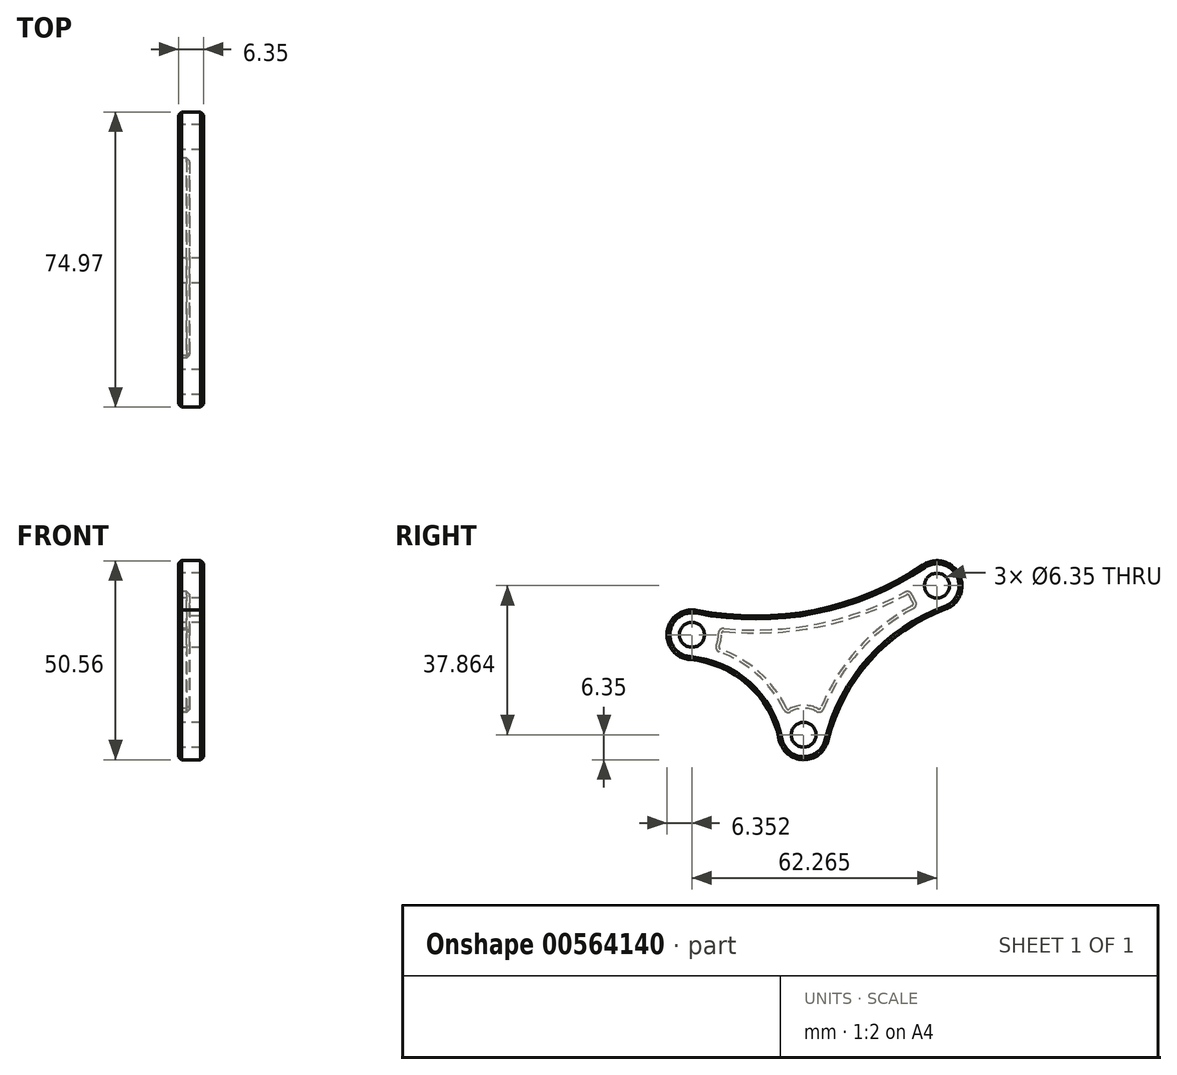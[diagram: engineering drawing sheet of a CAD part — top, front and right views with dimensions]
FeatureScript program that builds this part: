
annotation { "Feature Type Name" : "Feature", "Feature Type Description" : "" }
export const myFeature = defineFeature(function(context is Context, id is Id, definition is map)
    precondition{}
    {
        {
            var Q0;
            Q0=qCreatedBy(makeId("Right.planeOp"),FACE);
            var sketch = newSketch(context, id + "F0", { "sketchPlane" : qUnion([Q0])});
            skCircle(sketch, "E0", {"center": v(0, 0) * mm, "radius": 3.18 * mm});
            skCircle(sketch, "E1", {"center": v(33.87, 37.86) * mm, "radius": 3.18 * mm});
            skCircle(sketch, "E2", {"center": v(-28.4, 25.4) * mm, "radius": 3.18 * mm});
            skCircle(sketch, "E3", {"center": v(-28.4, 25.4) * mm, "radius": 6.35 * mm});
            skCircle(sketch, "E4", {"center": v(33.87, 37.86) * mm, "radius": 6.35 * mm});
            skCircle(sketch, "E5", {"center": v(0, 0) * mm, "radius": 6.35 * mm});
            skLineSegment(sketch, "E6", {"start": v(-28.4, 25.4) * mm, "end": v(33.87, 37.86) * mm});
            skLineSegment(sketch, "E7", {"start": v(0, 0) * mm, "end": v(-28.4, 25.4) * mm});
            skLineSegment(sketch, "E8", {"start": v(33.87, 37.86) * mm, "end": v(0, 0) * mm});
            skArc(sketch, "E9", {"start": v(-27.15, 31.63) * mm, "mid": v(2.73, 31.63) * mm, "end": v(30.32, 43.13) * mm});
            skArc(sketch, "E10", {"start": v(-6.23, -1.25) * mm, "mid": v(-14.2, 12.7) * mm, "end": v(-28.94, 19.07) * mm});
            skArc(sketch, "E11", {"start": v(36.05, 31.9) * mm, "mid": v(16.93, 18.93) * mm, "end": v(6.17, -1.5) * mm});
            skSolve(sketch);
        }
        {
            var Q0;
            {var subQ0=sQuery(id+"F0.wireOp",EDGE,"E9");var subQ1=sQuery(id+"F0.wireOp",EDGE,"E3");var subQ2=makeQuery(id+"F0.imprint","INTERSECT",VERTEX,{"derivedFrom":[subQ1,subQ0]});Q0=makeQuery(id+"F0.imprint","IMPRINT",FACE,{"disambiguationData":[TD([[makeQuery(id+"F0.imprint","IMPRINT",EDGE,{"disambiguationData":[TD([[subQ2,1.0]])],"derivedFrom":subQ1}),-1.0]])]});}
            var Q1;
            {var subQ0=sQuery(id+"F0.wireOp",EDGE,"E10");var subQ1=sQuery(id+"F0.wireOp",EDGE,"E3");var subQ2=makeQuery(id+"F0.imprint","INTERSECT",VERTEX,{"derivedFrom":[subQ1,subQ0]});Q1=makeQuery(id+"F0.imprint","IMPRINT",FACE,{"disambiguationData":[TD([[makeQuery(id+"F0.imprint","IMPRINT",EDGE,{"disambiguationData":[TD([[subQ2,-1.0]])],"derivedFrom":subQ1}),-1.0]])]});}
            var Q2;
            {var subQ0=sQuery(id+"F0.wireOp",EDGE,"E9");var subQ1=sQuery(id+"F0.wireOp",EDGE,"E4");var subQ2=makeQuery(id+"F0.imprint","INTERSECT",VERTEX,{"derivedFrom":[subQ1,subQ0]});Q2=makeQuery(id+"F0.imprint","IMPRINT",FACE,{"disambiguationData":[TD([[makeQuery(id+"F0.imprint","IMPRINT",EDGE,{"disambiguationData":[TD([[subQ2,-1.0]])],"derivedFrom":subQ1}),-1.0]])]});}
            var Q3;
            {var subQ0=sQuery(id+"F0.wireOp",EDGE,"E10");var subQ1=sQuery(id+"F0.wireOp",EDGE,"E5");var subQ2=makeQuery(id+"F0.imprint","INTERSECT",VERTEX,{"derivedFrom":[subQ1,subQ0]});Q3=makeQuery(id+"F0.imprint","IMPRINT",FACE,{"disambiguationData":[TD([[makeQuery(id+"F0.imprint","IMPRINT",EDGE,{"disambiguationData":[TD([[subQ2,1.0]])],"derivedFrom":subQ1}),-1.0]])]});}
            var Q4;
            {var subQ5=sQuery(id+"F0.wireOp",EDGE,"E7");var subQ6=sQuery(id+"F0.wireOp",EDGE,"E0");var subQ7=makeQuery(id+"F0.imprint","INTERSECT",VERTEX,{"derivedFrom":[subQ6,subQ5]});Q4=makeQuery(id+"F0.imprint","IMPRINT",FACE,{"disambiguationData":[TD([[makeQuery(id+"F0.imprint","IMPRINT",EDGE,{"disambiguationData":[TD([[subQ7,-1.0]])],"derivedFrom":subQ6}),-1.0]])]});}
            var Q5;
            {var subQ5=sQuery(id+"F0.wireOp",EDGE,"E6");var subQ7=sQuery(id+"F0.wireOp",EDGE,"E1");var subQ8=makeQuery(id+"F0.imprint","INTERSECT",VERTEX,{"derivedFrom":[subQ7,subQ5]});Q5=makeQuery(id+"F0.imprint","IMPRINT",FACE,{"disambiguationData":[TD([[makeQuery(id+"F0.imprint","IMPRINT",EDGE,{"disambiguationData":[TD([[subQ8,1.0]])],"derivedFrom":subQ7}),-1.0]])]});}
            var Q6;
            {var subQ4=sQuery(id+"F0.wireOp",EDGE,"E6");var subQ5=sQuery(id+"F0.wireOp",EDGE,"E2");var subQ6=makeQuery(id+"F0.imprint","INTERSECT",VERTEX,{"derivedFrom":[subQ5,subQ4]});Q6=makeQuery(id+"F0.imprint","IMPRINT",FACE,{"disambiguationData":[TD([[makeQuery(id+"F0.imprint","IMPRINT",EDGE,{"disambiguationData":[TD([[subQ6,-1.0]])],"derivedFrom":subQ5}),-1.0]])]});}
            var Q7;
            {var subQ0=sQuery(id+"F0.wireOp",EDGE,"E6");var subQ2=sQuery(id+"F0.wireOp",EDGE,"E3");var subQ3=makeQuery(id+"F0.imprint","INTERSECT",VERTEX,{"derivedFrom":[subQ2,subQ0]});Q7=makeQuery(id+"F0.imprint","IMPRINT",FACE,{"disambiguationData":[TD([[makeQuery(id+"F0.imprint","IMPRINT",EDGE,{"disambiguationData":[TD([[subQ3,1.0]])],"derivedFrom":subQ2}),-1.0]])]});}
            var Q8;
            {var subQ0=sQuery(id+"F0.wireOp",EDGE,"E6");var subQ1=sQuery(id+"F0.wireOp",EDGE,"E2");var subQ2=makeQuery(id+"F0.imprint","INTERSECT",VERTEX,{"derivedFrom":[subQ1,subQ0]});Q8=makeQuery(id+"F0.imprint","IMPRINT",FACE,{"disambiguationData":[TD([[makeQuery(id+"F0.imprint","IMPRINT",EDGE,{"disambiguationData":[TD([[subQ2,1.0]])],"derivedFrom":subQ1}),-1.0]])]});}
            var Q9;
            {var subQ0=sQuery(id+"F0.wireOp",EDGE,"E6");var subQ1=sQuery(id+"F0.wireOp",EDGE,"E1");var subQ2=makeQuery(id+"F0.imprint","INTERSECT",VERTEX,{"derivedFrom":[subQ1,subQ0]});Q9=makeQuery(id+"F0.imprint","IMPRINT",FACE,{"disambiguationData":[TD([[makeQuery(id+"F0.imprint","IMPRINT",EDGE,{"disambiguationData":[TD([[subQ2,-1.0]])],"derivedFrom":subQ1}),-1.0]])]});}
            var Q10;
            {var subQ0=sQuery(id+"F0.wireOp",EDGE,"E7");var subQ1=sQuery(id+"F0.wireOp",EDGE,"E0");var subQ2=makeQuery(id+"F0.imprint","INTERSECT",VERTEX,{"derivedFrom":[subQ1,subQ0]});Q10=makeQuery(id+"F0.imprint","IMPRINT",FACE,{"disambiguationData":[TD([[makeQuery(id+"F0.imprint","IMPRINT",EDGE,{"disambiguationData":[TD([[subQ2,1.0]])],"derivedFrom":subQ1}),-1.0]])]});}
            var Q11;
            {var subQ0=sQuery(id+"F0.wireOp",EDGE,"E11");var subQ1=sQuery(id+"F0.wireOp",EDGE,"E5");var subQ2=makeQuery(id+"F0.imprint","INTERSECT",VERTEX,{"derivedFrom":[subQ1,subQ0]});Q11=makeQuery(id+"F0.imprint","IMPRINT",FACE,{"disambiguationData":[TD([[makeQuery(id+"F0.imprint","IMPRINT",EDGE,{"disambiguationData":[TD([[subQ2,-1.0]])],"derivedFrom":subQ1}),-1.0]])]});}
            var Q12;
            {var subQ0=sQuery(id+"F0.wireOp",EDGE,"E11");var subQ1=sQuery(id+"F0.wireOp",EDGE,"E4");var subQ2=makeQuery(id+"F0.imprint","INTERSECT",VERTEX,{"derivedFrom":[subQ1,subQ0]});Q12=makeQuery(id+"F0.imprint","IMPRINT",FACE,{"disambiguationData":[TD([[makeQuery(id+"F0.imprint","IMPRINT",EDGE,{"disambiguationData":[TD([[subQ2,1.0]])],"derivedFrom":subQ1}),-1.0]])]});}
            var Q13;
            {var subQ7=sQuery(id+"F0.wireOp",EDGE,"s0z4VmjC-9Jtz-9oDN-pM9U-WHnKUmS6Y34w");Q13=makeQuery(id+"F0.imprint","IMPRINT",FACE,{"disambiguationData":[TD([[makeQuery(id+"F0.imprint","IMPRINT",EDGE,{"derivedFrom":subQ7}),-1.0]])]});}
            var Q14;
            {var subQ3=sQuery(id+"F0.wireOp",EDGE,"DwXPQsX5-wXzO-8GNt-yisA-XoadTiBy5RnP");Q14=makeQuery(id+"F0.imprint","IMPRINT",FACE,{"disambiguationData":[TD([[makeQuery(id+"F0.imprint","IMPRINT",EDGE,{"derivedFrom":subQ3}),1.0]])]});}
            extrude(context, id + "F1", {"entities" : qUnion([Q0, Q1, Q2, Q3, Q4, Q5, Q6, Q7, Q8, Q9, Q10, Q11, Q12, Q13, Q14]), "depth" : 6.35 * mm, "offsetDistance" : 25.4 * mm});
        }
        {
            var Q0;
            Q0=makeQuery(id+"F1.opExtrude","CAP_FACE",FACE,{"disambiguationData":[OSD([sQuery(id+"F0.wireOp",EDGE,"E0"),sQuery(id+"F0.wireOp",EDGE,"E1"),sQuery(id+"F0.wireOp",EDGE,"E2"),sQuery(id+"F0.wireOp",EDGE,"E3"),sQuery(id+"F0.wireOp",EDGE,"E4"),sQuery(id+"F0.wireOp",EDGE,"E5"),sQuery(id+"F0.wireOp",EDGE,"E9"),sQuery(id+"F0.wireOp",EDGE,"E10"),sQuery(id+"F0.wireOp",EDGE,"E11")])],"isStart":true});
            shell(context, id + "F2", {"entities" : qUnion([Q0]), "thickness" : 3.56 * mm});
        }
        {
            var Q0;
            Q0=makeQuery(id+"F2.opShell","TWEAK_EDGE",EDGE,{"derivedFrom":[makeQuery(id+"F1.opExtrude","SWEPT_FACE",FACE,{"disambiguationData":[OSD([sQuery(id+"F0.wireOp",EDGE,"E2")])]}),makeQuery(id+"F1.opExtrude","SWEPT_FACE",FACE,{"disambiguationData":[OSD([sQuery(id+"F0.wireOp",EDGE,"E9")])]})]});
            var Q1;
            Q1=makeQuery(id+"F2.opShell","TWEAK_EDGE",EDGE,{"derivedFrom":[makeQuery(id+"F1.opExtrude","SWEPT_FACE",FACE,{"disambiguationData":[OSD([sQuery(id+"F0.wireOp",EDGE,"E2")])]}),makeQuery(id+"F1.opExtrude","SWEPT_FACE",FACE,{"disambiguationData":[OSD([sQuery(id+"F0.wireOp",EDGE,"E10")])]})]});
            var Q2;
            Q2=makeQuery(id+"F2.opShell","TWEAK_EDGE",EDGE,{"derivedFrom":[makeQuery(id+"F1.opExtrude","SWEPT_FACE",FACE,{"disambiguationData":[OSD([sQuery(id+"F0.wireOp",EDGE,"E0")])]}),makeQuery(id+"F1.opExtrude","SWEPT_FACE",FACE,{"disambiguationData":[OSD([sQuery(id+"F0.wireOp",EDGE,"E10")])]})]});
            var Q3;
            Q3=makeQuery(id+"F2.opShell","TWEAK_EDGE",EDGE,{"derivedFrom":[makeQuery(id+"F1.opExtrude","SWEPT_FACE",FACE,{"disambiguationData":[OSD([sQuery(id+"F0.wireOp",EDGE,"E0")])]}),makeQuery(id+"F1.opExtrude","SWEPT_FACE",FACE,{"disambiguationData":[OSD([sQuery(id+"F0.wireOp",EDGE,"E11")])]})]});
            var Q4;
            Q4=makeQuery(id+"F2.opShell","TWEAK_EDGE",EDGE,{"derivedFrom":[makeQuery(id+"F1.opExtrude","SWEPT_FACE",FACE,{"disambiguationData":[OSD([sQuery(id+"F0.wireOp",EDGE,"E1")])]}),makeQuery(id+"F1.opExtrude","SWEPT_FACE",FACE,{"disambiguationData":[OSD([sQuery(id+"F0.wireOp",EDGE,"E9")])]})]});
            var Q5;
            Q5=makeQuery(id+"F2.opShell","TWEAK_EDGE",EDGE,{"derivedFrom":[makeQuery(id+"F1.opExtrude","SWEPT_FACE",FACE,{"disambiguationData":[OSD([sQuery(id+"F0.wireOp",EDGE,"E1")])]}),makeQuery(id+"F1.opExtrude","SWEPT_FACE",FACE,{"disambiguationData":[OSD([sQuery(id+"F0.wireOp",EDGE,"E11")])]})]});
            fillet(context, id + "F3", {"entities" : qUnion([Q0, Q1, Q2, Q3, Q4, Q5]), "radius" : 1.27 * mm, "tangentPropagation" : true, "allowEdgeOverflow" : false});
        }
        {
            var Q0;
            Q0=makeQuery(id+"F1.opExtrude","CAP_EDGE",EDGE,{"disambiguationData":[OSD([sQuery(id+"F0.wireOp",EDGE,"E9")])],"isStart":false});
            var Q1;
            {var subQ0=sQuery(id+"F0.wireOp",EDGE,"E10");Q1=makeQuery(id+"F2.opShell","OFFSET_EDGE",EDGE,{"disambiguationData":[OSD([subQ0]),TDD([makeQuery(id+"F1.opExtrude","CAP_EDGE",EDGE,{"disambiguationData":[OSD([subQ0])],"isStart":false})])]});}
            var Q2;
            Q2=makeQuery(id+"F1.opExtrude","CAP_EDGE",EDGE,{"disambiguationData":[OSD([sQuery(id+"F0.wireOp",EDGE,"E9")])],"isStart":true});
            chamfer(context, id + "F4", {"entities" : qUnion([Q0, Q1, Q2]), "width" : 0.76 * mm, "tangentPropagation" : true});
        }
    });
